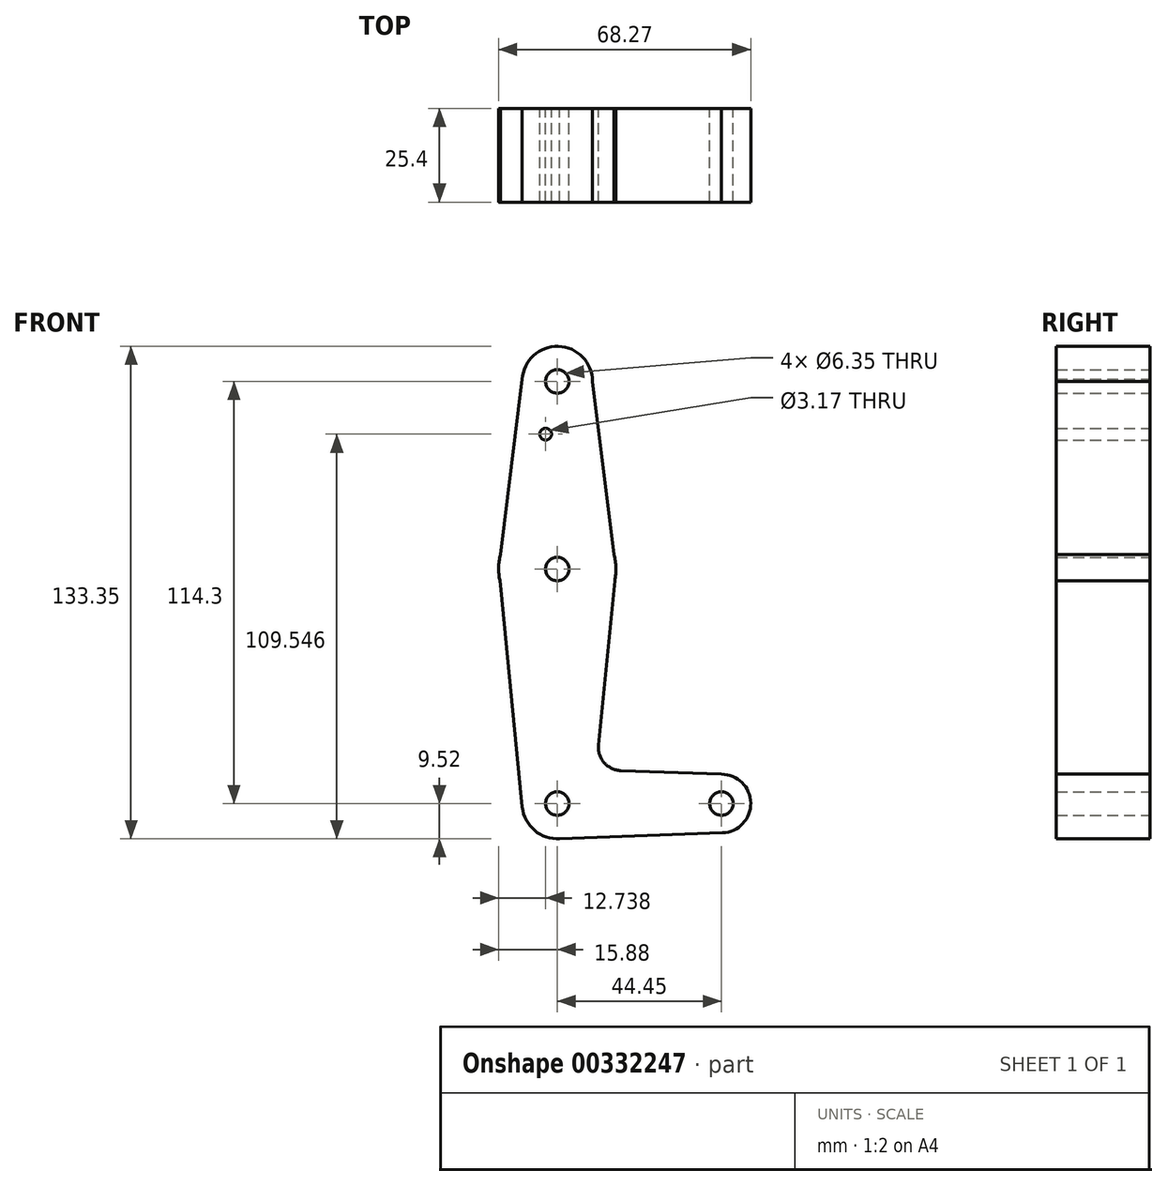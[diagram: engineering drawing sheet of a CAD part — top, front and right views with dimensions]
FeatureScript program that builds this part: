
annotation { "Feature Type Name" : "Feature", "Feature Type Description" : "" }
export const myFeature = defineFeature(function(context is Context, id is Id, definition is map)
    precondition{}
    {
        {
            var Q0;
            Q0=qCreatedBy(makeId("Front.planeOp"),FACE);
            var sketch = newSketch(context, id + "F0", { "sketchPlane" : qUnion([Q0])});
            skLineSegment(sketch, "E0", {"start": v(0, 0) * mm, "end": v(0, -56.85) * mm, "construction": true});
            skLineSegment(sketch, "E1", {"start": v(0, -56.85) * mm, "end": v(44.45, -56.85) * mm, "construction": true});
            skLineSegment(sketch, "E2", {"start": v(0, 0) * mm, "end": v(0, 57.45) * mm, "construction": true});
            skCircle(sketch, "E3", {"center": v(0, 57.45) * mm, "radius": 9.53 * mm});
            skCircle(sketch, "E4", {"center": v(0, 6.65) * mm, "radius": 15.88 * mm});
            skCircle(sketch, "E5", {"center": v(0, -56.85) * mm, "radius": 9.53 * mm});
            skCircle(sketch, "E6", {"center": v(44.45, -56.85) * mm, "radius": 7.94 * mm});
            skLineSegment(sketch, "E7", {"start": v(-9.5, 58.02) * mm, "end": v(-15.87, 6.65) * mm});
            skLineSegment(sketch, "E8", {"start": v(-15.87, 6.65) * mm, "end": v(-9.48, -57.8) * mm});
            skLineSegment(sketch, "E9", {"start": v(9.52, 57.45) * mm, "end": v(15.88, 6.65) * mm});
            skLineSegment(sketch, "E10", {"start": v(15.88, 6.65) * mm, "end": v(11.15, -40.96) * mm});
            skLineSegment(sketch, "E11", {"start": v(44.45, -48.91) * mm, "end": v(17.24, -47.94) * mm});
            skLineSegment(sketch, "E12", {"start": v(0, -66.37) * mm, "end": v(44.73, -64.78) * mm});
            skCircle(sketch, "E13", {"center": v(0, 57.45) * mm, "radius": 3.18 * mm});
            skCircle(sketch, "E14", {"center": v(0, 6.65) * mm, "radius": 3.18 * mm});
            skCircle(sketch, "E15", {"center": v(-3.14, 43.18) * mm, "radius": 1.59 * mm});
            skCircle(sketch, "E16", {"center": v(0, -56.85) * mm, "radius": 3.18 * mm});
            skCircle(sketch, "E17", {"center": v(44.45, -56.85) * mm, "radius": 3.18 * mm});
            skPoint(sketch, "E18.newPointA", {"position": v(0, -47.32) * mm});
            skArc(sketch, "E18.filletArc", {"start": v(11.15, -40.96) * mm, "mid": v(12.69, -45.77) * mm, "end": v(17.24, -47.94) * mm});
            skSolve(sketch);
        }
        {
            var Q0;
            Q0=qSketchRegion(id+"F0",true);
            extrude(context, id + "F1", {"entities" : qUnion([Q0]), "depth" : 25.4 * mm});
        }
    });
